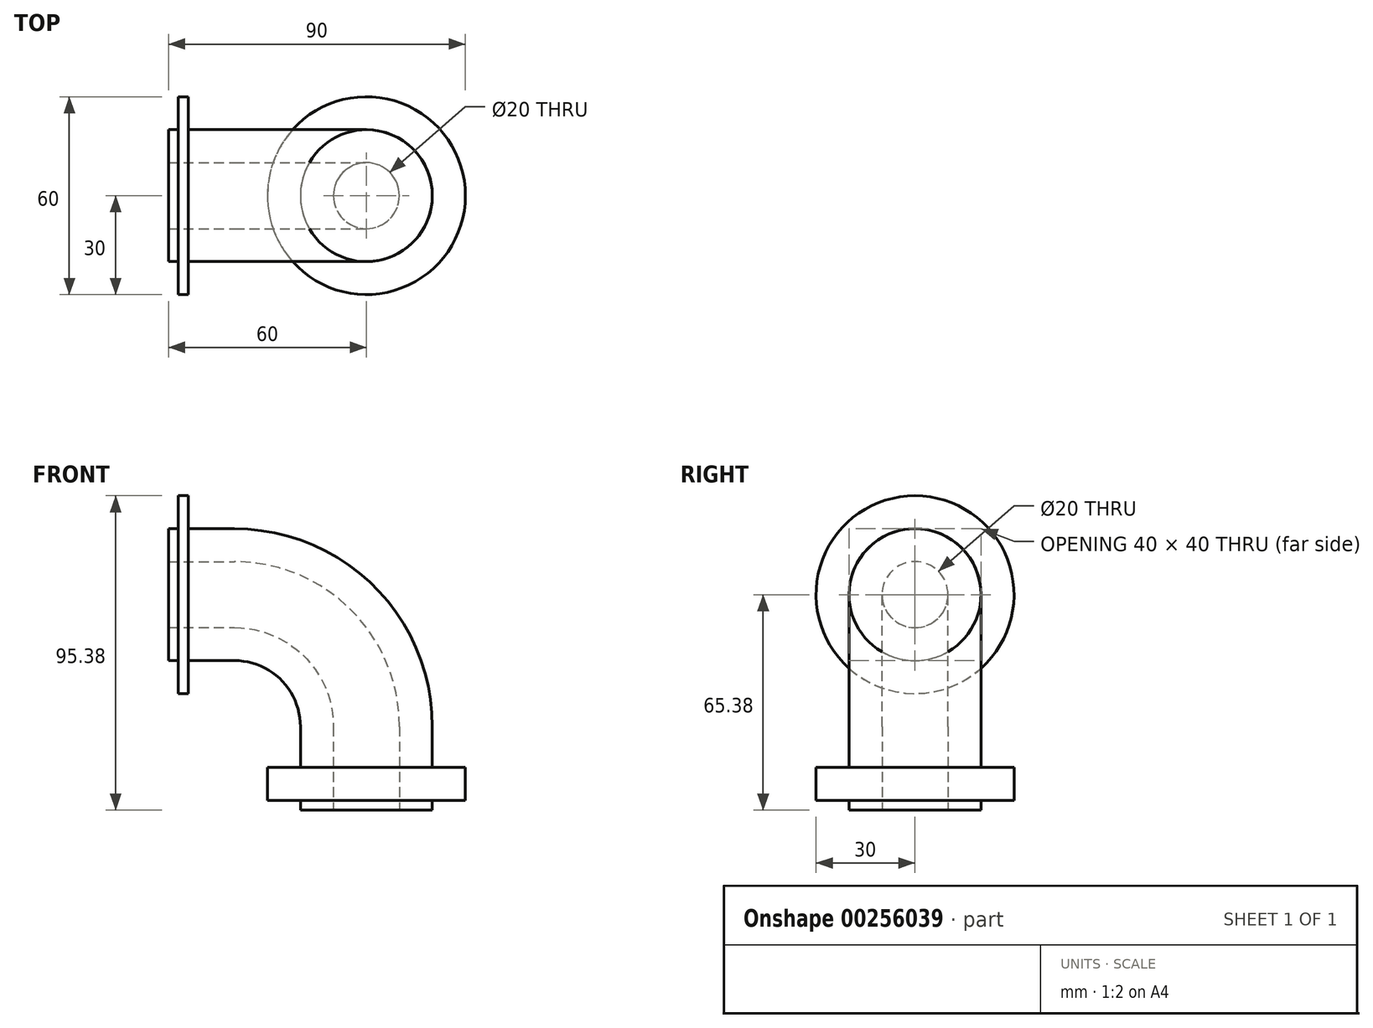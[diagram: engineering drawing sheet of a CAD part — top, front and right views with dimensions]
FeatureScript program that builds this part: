
annotation { "Feature Type Name" : "Feature", "Feature Type Description" : "" }
export const myFeature = defineFeature(function(context is Context, id is Id, definition is map)
    precondition{}
    {
        {
            var Q0;
            Q0=qCreatedBy(makeId("Right.planeOp"),FACE);
            var sketch = newSketch(context, id + "F0", { "sketchPlane" : qUnion([Q0])});
            skCircle(sketch, "E0", {"center": v(0, 0) * mm, "radius": 10 * mm});
            skCircle(sketch, "E1", {"center": v(0, 0) * mm, "radius": 20 * mm});
            skSolve(sketch);
        }
        {
            var Q0;
            Q0=qCreatedBy(makeId("Front.planeOp"),FACE);
            var sketch = newSketch(context, id + "F1", { "sketchPlane" : qUnion([Q0])});
            skLineSegment(sketch, "E2", {"start": v(0, 0) * mm, "end": v(20, 0) * mm});
            skArc(sketch, "E3", {"start": v(20, 0) * mm, "mid": v(48.28, -11.72) * mm, "end": v(60, -40) * mm});
            skLineSegment(sketch, "E4", {"start": v(60, -40) * mm, "end": v(60, -65.38) * mm});
            skSolve(sketch);
        }
        {
            var Q0;
            Q0=makeQuery(id+"F0.imprint","IMPRINT",FACE,{"disambiguationData":[TD([[makeQuery(id+"F0.imprint","IMPRINT",EDGE,{"derivedFrom":sQuery(id+"F0.wireOp",EDGE,"E0")}),-1.0]])]});
            var Q1;
            Q1=sQuery(id+"F1.wireOp",EDGE,"E2");
            var Q2;
            Q2=sQuery(id+"F1.wireOp",EDGE,"E3");
            var Q3;
            Q3=sQuery(id+"F1.wireOp",EDGE,"E4");
            sweep(context, id + "F2", {"profiles" : qUnion([Q0]), "path" : qUnion([Q1, Q2, Q3])});
        }
        {
            var Q0;
            Q0=makeQuery(id+"F2.opSweep","CAP_FACE",FACE,{"disambiguationData":[OSD([sQuery(id+"F0.wireOp",EDGE,"E0"),sQuery(id+"F0.wireOp",EDGE,"E1"),sQuery(id+"F1.wireOp",VERTEX,"E2.start")])],"isStart":true});
            cPlane(context, id + "F3", {"entities" : qUnion([Q0]), "cplaneType" : CPlaneType.OFFSET, "offset" : 3 * mm, "oppositeDirection" : true, "width" : 150 * mm, "height" : 150 * mm});
        }
        {
            var Q0;
            Q0=qCreatedBy(id+"F3.planeOp",FACE);
            var sketch = newSketch(context, id + "F4", { "sketchPlane" : qUnion([Q0])});
            skCircle(sketch, "E5", {"center": v(0, 0) * mm, "radius": 30 * mm});
            skCircle(sketch, "E6.0", {"center": v(0, 0) * mm, "radius": 20 * mm});
            skSolve(sketch);
        }
        {
            var Q0;
            Q0=makeQuery(id+"F4.imprint","IMPRINT",FACE,{"disambiguationData":[TD([[makeQuery(id+"F4.imprint","IMPRINT",EDGE,{"derivedFrom":sQuery(id+"F4.wireOp",EDGE,"E5")}),1.0]])]});
            extrude(context, id + "F5", {"entities" : qUnion([Q0]), "operationType" : NewBodyOperationType.ADD, "oppositeDirection" : true, "depth" : 3 * mm});
        }
        {
            var Q0;
            Q0=makeQuery(id+"F2.opSweep","CAP_FACE",FACE,{"disambiguationData":[OSD([sQuery(id+"F0.wireOp",EDGE,"E0"),sQuery(id+"F0.wireOp",EDGE,"E1"),sQuery(id+"F1.wireOp",VERTEX,"E4.end")])],"isStart":false});
            cPlane(context, id + "F6", {"entities" : qUnion([Q0]), "cplaneType" : CPlaneType.OFFSET, "offset" : 3 * mm, "oppositeDirection" : true, "width" : 150 * mm, "height" : 150 * mm});
        }
        {
            var Q0;
            Q0=qCreatedBy(id+"F6.planeOp",FACE);
            var sketch = newSketch(context, id + "F7", { "sketchPlane" : qUnion([Q0])});
            skCircle(sketch, "E7.0.0", {"center": v(60, 0) * mm, "radius": 20 * mm});
            skCircle(sketch, "E8", {"center": v(60, 0) * mm, "radius": 30 * mm});
            skSolve(sketch);
        }
        {
            var Q0;
            Q0 = qSketchRegion(id + "F7", true);
            extrude(context, id + "F8", {"entities" : qUnion([Q0]), "operationType" : NewBodyOperationType.ADD, "oppositeDirection" : true, "depth" : 10 * mm});
        }
    });
